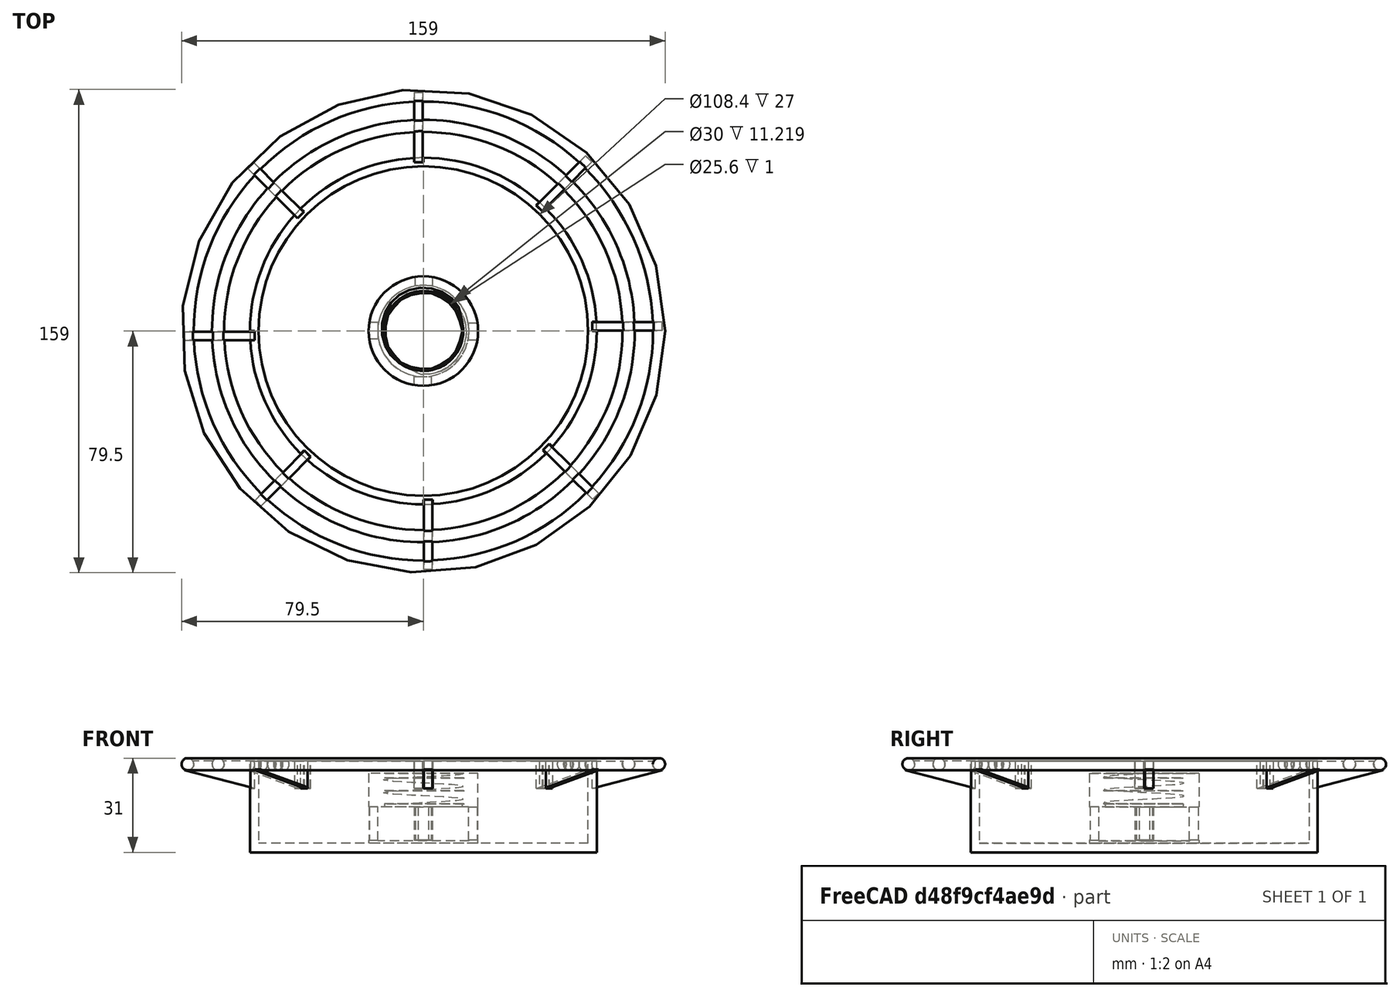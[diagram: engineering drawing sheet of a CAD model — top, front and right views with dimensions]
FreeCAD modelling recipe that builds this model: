
FCSTD DOCUMENT  (FreeCAD 0.20R29177 +426 (Git))
Label: feeder-bottom
License: All rights reserved
LicenseURL: http://en.wikipedia.org/wiki/All_rights_reserved
objects: PartDesign::AdditiveCylinder×3, PartDesign::SubtractiveCylinder×3, PartDesign::PolarPattern×3, PartDesign::SubtractiveBox×2, PartDesign::Body×2, PartDesign::AdditiveTorus×2, Part::Part2DObjectPython×1, Part::Helix×1, PartDesign::SubtractivePipe×1, PartDesign::AdditiveWedge×1
note: 31 computed .brp shape members not serialized (recipe doc carries the construction recipe); baked Part::Feature solids carry a one-line shape summary decoded from their .brp

FEATURE [PartDesign::AdditiveCylinder] Cylinder
  Angle = 360
  AttacherType = Attacher::AttachEngine3D
  FirstAngle = 0
  Height = 30
  MapMode = 5
  Radius = 57
  SecondAngle = 0
  Support = -> [XY_Plane]
  expr: Radius = 114 / 2
FEATURE [PartDesign::SubtractiveCylinder] Cylinder001
  Angle = 360
  AttacherType = Attacher::AttachEngine3D
  AttachmentOffset = pos=(0,0,-27) rot=(0,0,1;0rad)
  BaseFeature = -> Cylinder
  FirstAngle = 0
  Height = 27
  MapMode = 5
  Placement = pos=(0,0,3) rot=(0,0,1;0rad)
  Radius = 54.2
  SecondAngle = 0
  Support = -> [Cylinder]
  expr: .AttachmentOffset.Base.z = -Height
  expr: Radius = 108.4 / 2
FEATURE [PartDesign::SubtractiveBox] Box
  AttacherType = Attacher::AttachEngine3D
  AttachmentOffset = pos=(0,-57,-9) rot=(0,0,1;0rad)
  BaseFeature = -> Cylinder001
  Height = 9.5
  Length = 3.05
  MapMode = 11
  Placement = pos=(57,-1.27e-14,21) rot=(0,0,1;1.5708rad)
  Support = -> [Cylinder001]
  Width = 1.5
FEATURE [PartDesign::PolarPattern] PolarPattern
  Angle = 360
  Axis = -> Z_Axis
  BaseFeature = -> Box
  Occurrences = 8
  Originals = -> [Box]
  Placement = pos=(57,-1.27e-14,21) rot=(0,0,1;1.5708rad)
FEATURE [PartDesign::AdditiveCylinder] Cylinder002
  Angle = 360
  AttacherType = Attacher::AttachEngine3D
  AttachmentOffset = pos=(0,0,2.8) rot=(0,0,1;0rad)
  BaseFeature = -> PolarPattern
  FirstAngle = 0
  Height = 12.7
  MapMode = 5
  Placement = pos=(0,0,2.8) rot=(0,0,1;0rad)
  Radius = 18
  SecondAngle = 0
  Support = -> [XY_Plane]
  expr: Height = 23.5 - 10.8
  expr: Radius = 36 / 2
FEATURE [PartDesign::SubtractiveCylinder] Cylinder003
  Angle = 360
  AttacherType = Attacher::AttachEngine3D
  AttachmentOffset = pos=(0,0,-11) rot=(0,0,1;0rad)
  BaseFeature = -> Cylinder002
  FirstAngle = 0
  Height = 12.7
  MapMode = 45
  Placement = pos=(-7.1e-15,1.09e-14,3.78081) rot=(0,0,1;0rad)
  Radius = 15
  SecondAngle = 0
  Support = -> [Cylinder002]
  expr: Height = <<Cylinder002>>.Height
  expr: Radius = <<Cylinder002>>.Radius - 3mm
FEATURE [PartDesign::SubtractiveBox] Box001
  AttacherType = Attacher::AttachEngine3D
  AttachmentOffset = pos=(-18,4,-3) rot=(0,0,1;0rad)
  BaseFeature = -> Cylinder003
  Height = 5.6
  Length = 3.1
  MapMode = 5
  Placement = pos=(-18,3,4) rot=(1,0,0;1.5708rad)
  Support = -> [XZ_Plane]
  Width = 22
FEATURE [PartDesign::PolarPattern] PolarPattern001
  Angle = 360
  Axis = -> Z_Axis
  BaseFeature = -> Box001
  Occurrences = 4
  Originals = -> [Box001]
  Placement = pos=(-18,3,4) rot=(1,0,0;1.5708rad)
FEATURE [PartDesign::AdditiveCylinder] Cylinder004
  Angle = 360
  AttacherType = Attacher::AttachEngine3D
  AttachmentOffset = pos=(0,0,15) rot=(0,0,1;0rad)
  BaseFeature = -> PolarPattern001
  FirstAngle = 0
  Height = 11
  MapMode = 5
  Placement = pos=(0,0,15) rot=(0,0,1;0rad)
  Radius = 18
  SecondAngle = 0
  Support = -> [XY_Plane]
  expr: Radius = Cylinder002.Radius
FEATURE [PartDesign::SubtractiveCylinder] Cylinder005
  Angle = 360
  AttacherType = Attacher::AttachEngine3D
  AttachmentOffset = pos=(0,0,-11) rot=(0,0,1;0rad)
  BaseFeature = -> Cylinder004
  FirstAngle = 0
  Height = 11
  MapMode = 5
  Placement = pos=(0,0,15) rot=(0,0,1;0rad)
  Radius = 12.8
  SecondAngle = 0
  Support = -> [Cylinder004]
  expr: .AttachmentOffset.Base.z = -Height
  expr: Height = Cylinder004.Height
  expr: Radius = 25.6 / 2
FEATURE [Part::Part2DObjectPython] Bottle_M_ThreadProfile  # Draft 2D object (typed FeaturePython)
  Area = 581.874
  Closed = true
  Continuity = C2
  Height = 10
  Helix = Helix
  Instructions = Expand this with the ... button to view instructions | Sweep this object along a helix of the same pitch to produce your thread. | It is recommended to make the helix in the ThreadProfile workbench. | If there is an active Body the ThreadProfile object will be put into it.,If not it can be dragged and dropped into the body later. | If there is an active Body when the helix is made there will be made a ShapeBinder for it | For internal threads you will need to cut the Sweep object out of a cylinder, or if using Part Design sweep it as a Subtractive Pipe. | Always use Frenet mode | I have provided some presets, but it is possible there could be some errors.  Double check for mission critical applications. | Also, the tolerances might be different from what you wish to have.  I believe the internal minor diameters are all minimum and the external are all maximum.
  InternalOrExternal = 1
  MakeFace = true
  MinorDiameter = 26.23
  Parameterization = 1
  Pitch = 4.23333
  Placement = pos=(0,0,26) rot=(0,0,1;0rad)
  Points = (120) [(13.0973,0.687355,0),(13.0466,1.37318,0),(12.965,2.05636,0),(12.8537,2.73605,0),(12.7134,3.4115,0),(12.5467,4.08274,0),(12.3607,4.75205,0),+113 more]
  Presets = 8
  Quality = 6
  ThreadCount = 2.3622
  Variants = 0
  Version = 1.89
  external2S_data = [-0.00461051,-0.00886426,-0.0128148,-0.0165028,-0.0199596,-0.0232105,-0.0262759,-0.0291725,-0.0319145,-0.0345137,-0.0369805,-0.0393235,-0.0415505,-0.0436681,-0.0456823,-0.0475981,-0.0494204,-0.0511532,-0.0528003,-0.0543649,-0.0558502,+698 more]
  external3S_data = [-0.00677828,-0.0128149,-0.0182584,-0.0232106,-0.0277444,-0.0319145,-0.0357632,-0.0393236,-0.0426227,-0.0456823,-0.0485208,-0.0511533,-0.0535928,-0.0558503,-0.0579353,-0.059856,-0.0616195,-0.0632319,-0.0646984,-0.0660239,-0.0672123,+698 more]
  external45_data = [-0.00137363,-0.00271738,-0.00403219,-0.00531893,-0.00657844,-0.00781148,-0.00901878,-0.010201,-0.0113589,-0.012493,-0.0136039,-0.0146921,-0.0157583,-0.0168028,-0.0178261,-0.0188288,-0.0198112,-0.0207738,-0.0217169,-0.0226409,-0.0235462,+698 more]
  external_data = [6.8683e-05,0.000137366,0.000212133,0.000297079,0.000434727,0.000654671,0.000874565,0.00109436,0.00135915,0.00172112,0.00208281,0.0024438,0.00285056,0.00336131,0.0038717,0.00438141,0.0049559,0.00562874,0.00630075,0.00697193,0.00775661,+698 more]
  internal2S_data = [0,0,0,0,0,0,0,0,0,0,0,0,0,0,0,0,0,0,0,0,0,0,0,0,0,0,0,0,0,0,0,0,0,0,0,0,0,0,0,0,0,0,0,0,0,0,0,0,0,0,0,0,0,0,0,0,0,0,0,0,0,0,0,0,0,0,0,0,0,0,0,0,0,0,0,0,0,0,0,0,0,0,0,0,0,0,0,0,0,0,0.00481128,0.00962256,0.0144338,0.0192451,0.0240564,+624 more]
  internal3S_data = [0,0,0,0,0,0,0,0,0,0,0,0,0,0,0,0,0,0,0,0,0,0,0,0,0,0,0,0,0,0,0,0,0,0,0,0,0,0,0,0,0,0,0,0,0,0,0,0,0,0,0,0,0,0,0,0,0,0,0,0,0.00721688,0.0144338,0.0216506,0.0288675,0.0360844,0.0433013,0.0505181,0.057735,0.0649519,0.0721688,0.0793857,0.0866025,+647 more]
  internal45_data = [0,0,0,0,0,0,0,0,0,0,0,0,0,0,0,0,0,0,0,0,0,0,0,0,0,0,0,0,0,0,0,0,0,0,0,0,0,0,0,0,0,0,0,0,0,0,0,0,0,0,0,0,0,0,0,0,0,0,0,0,0,0,0,0,0,0,0,0,0,0,0,0,0,0,0,0,0,0,0,0,0,0,0,0,0,0,0,0,0,0,0,0,0,0,0,0,0,0,0,0,0,0,0,0,0,0,0,0,0,0,0,0,0,0,0,0,0,0,0,0,+599 more]
  internal_data = [6.8683e-05,0.000137366,0.000212133,0.000297079,0.000434727,0.000654671,0.000874565,0.00109436,0.00135915,0.00172112,0.00208281,0.0024438,0.00285056,0.00336131,0.0038717,0.00438141,0.0049559,0.00562874,0.00630075,0.00697193,0.00775661,+698 more]
  preset_names = Bottle presets | 13-SP415(M) 2.1166666666666667 | 15-SP415(M) 2.1166666666666667 | 18-SP400(M) 3.175 | 20-SP400(M) 3.175 | 22-SP400(M) 3.175 | 24-SP400(M) 3.175 | 28-SP400(M) 4.233333333333333 | 30-SP400(M) 4.233333333333333 | 33-SP400(M) 4.233333333333333 | 35-SP400(M) 4.233333333333333 | 38-SP400(M) 4.233333333333333 | 40-SP400(M) 4.233333333333333 | 43-SP400(M) 4.233333333333333 | 45-SP400(M) 4.233333333333333 | 48-SP400(M) 4.233333333333333 | 51-SP400(M) 4.233333333333333 | 53-SP400(M) 4.233333333333333 | 58-SP400(M) 4.233333333333333 | 60-SP400(M) 4.233333333333333 | 63-SP400(M) 4.233333333333333 | 66-SP400(M) 4.233333333333333 | 70-SP400(M) 4.233333333333333 | 75-SP400(M) 4.233333333333333 | 77-SP400(M) 4.233333333333333 | 83-SP400(M) 5.08 | 89-SP400(M) 5.08 | 100-SP400(M) 5.08 | 110-SP400(M) 5.08 | 120-SP400(M) 5.08
  presets_data = [0,0,0,2.11667,11.53,11.78,2.11667,13.23,13.48,3.175,15.75,16,3.175,17.75,18,3.175,19.76,20.01,3.175,21.74,21.99,4.23333,25.25,25.5,4.23333,26.23,26.48,4.23333,29.74,29.99,4.23333,32.25,32.5,4.23333,35.1,35.35,4.23333,37.75,38,4.23333,39.62,+49 more]
FEATURE [Part::Helix] Helix
  Angle = 0
  AttacherType = Attacher::AttachEngine3D
  Height = 10
  LocalCoord = 0
  Pitch = 4.23333
  Radius = 1
  SegmentLength = 1
  Style = 0
  expr: AttachmentOffset = Bottle_M_ThreadProfile.AttachmentOffset
  expr: Height = Bottle_M_ThreadProfile.ThreadCount * Bottle_M_ThreadProfile.Pitch
  expr: MapMode = Bottle_M_ThreadProfile.MapMode
  expr: MapPathParameter = Bottle_M_ThreadProfile.MapPathParameter
  expr: MapReversed = Bottle_M_ThreadProfile.MapReversed
  expr: Pitch = Bottle_M_ThreadProfile.Pitch
  expr: SegmentLength = 1
  expr: Support = Bottle_M_ThreadProfile.Support
FEATURE [PartDesign::SubtractivePipe] SubtractivePipe
  AuxilleryCurvelinear = true
  AuxillerySpineTangent = false
  BaseFeature = -> Cylinder005
  Binormal = (0,0,0)
  Mode = 2
  Placement = pos=(0,0,15) rot=(0,0,1;0rad)
  Profile = -> Bottle_M_ThreadProfile
  Spine = -> Helix [Edge1,Edge2,Edge3]
  SpineTangent = false
  Transformation = 0
  Transition = 0
FEATURE [PartDesign::Body] Body  label="feeder-bottom"
  Group = -> [Cylinder,Cylinder001,Box,PolarPattern,Cylinder002,Cylinder003,Box001,PolarPattern001,Cylinder004,Cylinder005,Bottle_M_ThreadProfile,Helix,SubtractivePipe]
  Origin = -> Origin
  Tip = -> SubtractivePipe
FEATURE [PartDesign::AdditiveWedge] Wedge
  AttacherType = Attacher::AttachEngine3D
  AttachmentOffset = pos=(3,4,0) rot=(0,-0.707107,-0.707107;3.14159rad)
  MapMode = 5
  Placement = pos=(55.5,3,19) rot=(0,0,-1;1.5708rad)
  Support = -> [SubtractivePipe]
  X2max = 2.8
  X2min = 0
  Xmax = 2.8
  Xmin = 0
  Ymax = 23
  Ymin = 0
  Z2max = 11
  Z2min = 8
  Zmax = 11
  Zmin = 2
FEATURE [PartDesign::AdditiveTorus] Torus
  Angle1 = -180
  Angle2 = 180
  Angle3 = 360
  AttacherType = Attacher::AttachEngine3D
  AttachmentOffset = pos=(0,0,29) rot=(0,0,1;0rad)
  BaseFeature = -> Wedge
  MapMode = 5
  Placement = pos=(0,0,29) rot=(0,0,1;0rad)
  Radius1 = 77.5
  Radius2 = 2
  Support = -> [XY_Plane001]
  expr: Radius1 = 155 / 2
FEATURE [PartDesign::PolarPattern] PolarPattern002
  Angle = 360
  Axis = -> Z_Axis001
  BaseFeature = -> Torus
  Occurrences = 8
  Originals = -> [Wedge]
  Placement = pos=(0,0,29) rot=(0,0,1;0rad)
FEATURE [PartDesign::AdditiveTorus] Torus001
  Angle1 = -180
  Angle2 = 180
  Angle3 = 360
  AttacherType = Attacher::AttachEngine3D
  AttachmentOffset = pos=(0,0,29) rot=(0,0,1;0rad)
  BaseFeature = -> PolarPattern002
  MapMode = 5
  Placement = pos=(0,0,29) rot=(0,0,1;0rad)
  Radius1 = 67.5
  Radius2 = 2
  Support = -> [XY_Plane001]
  expr: Radius1 = 135 / 2
FEATURE [PartDesign::Body] Body001  label="perch"
  Group = -> [Wedge,Torus,PolarPattern002,Torus001]
  Origin = -> Origin001
  Tip = -> Torus001
